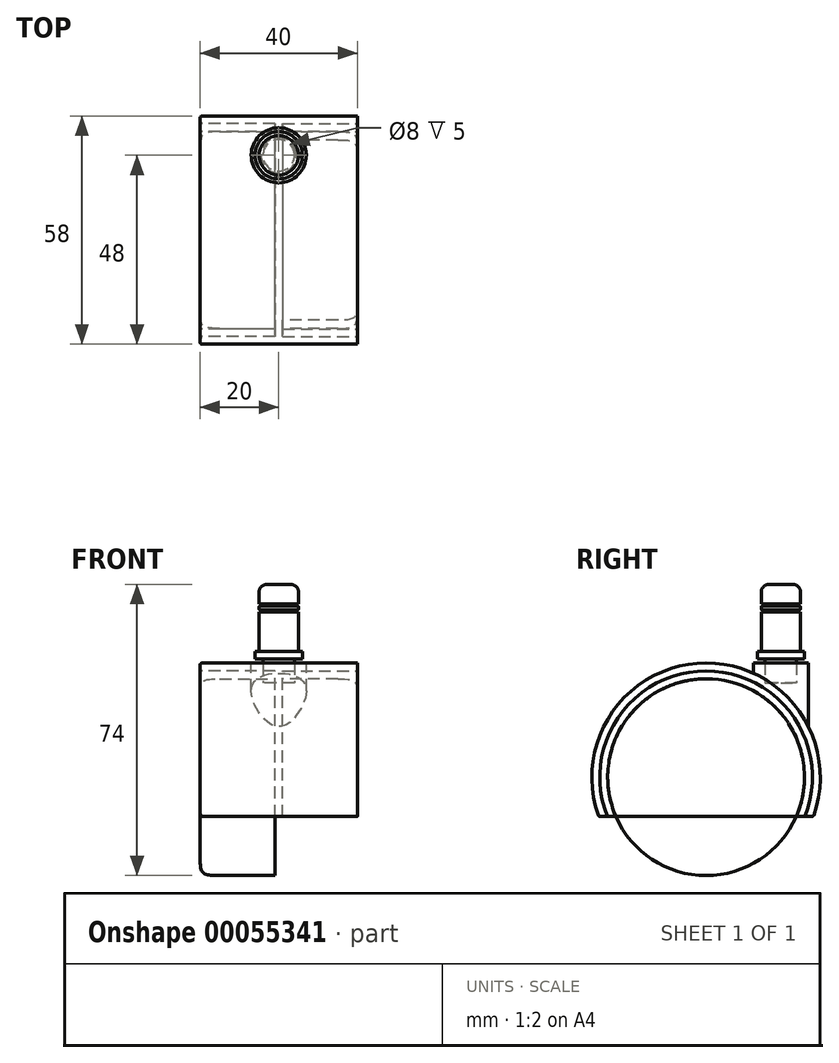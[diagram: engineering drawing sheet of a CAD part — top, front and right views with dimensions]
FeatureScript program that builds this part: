
annotation { "Feature Type Name" : "Feature", "Feature Type Description" : "" }
export const myFeature = defineFeature(function(context is Context, id is Id, definition is map)
    precondition{}
    {
        {
            var Q0;
            Q0=qCreatedBy(makeId("Top.planeOp"),FACE);
            var sketch = newSketch(context, id + "F0", { "sketchPlane" : qUnion([Q0])});
            skLineSegment(sketch, "E0.rect.bottom", {"start": v(20, -29) * mm, "end": v(-20, -29) * mm});
            skLineSegment(sketch, "E0.rect.top", {"start": v(20, 29) * mm, "end": v(-20, 29) * mm});
            skLineSegment(sketch, "E0.rect.left", {"start": v(20, -29) * mm, "end": v(20, 29) * mm});
            skLineSegment(sketch, "E0.rect.right", {"start": v(-20, -29) * mm, "end": v(-20, 29) * mm});
            skPoint(sketch, "E0.rect.middle", {"position": v(0, 0) * mm});
            skLineSegment(sketch, "E1", {"start": v(0, 0) * mm, "end": v(0, 19) * mm, "construction": true});
            skCircle(sketch, "E2", {"center": v(0, 19) * mm, "radius": 7 * mm});
            skSolve(sketch);
        }
        {
            var Q0;
            Q0=makeQuery(id+"F0.imprint","IMPRINT",FACE,{"disambiguationData":[TD([[makeQuery(id+"F0.imprint","IMPRINT",EDGE,{"derivedFrom":sQuery(id+"F0.wireOp",EDGE,"E0.rect.bottom")}),-1.0]])]});
            var Q1;
            Q1=makeQuery(id+"F0.imprint","IMPRINT",FACE,{"disambiguationData":[TD([[makeQuery(id+"F0.imprint","IMPRINT",EDGE,{"derivedFrom":sQuery(id+"F0.wireOp",EDGE,"E2")}),1.0]])]});
            extrude(context, id + "F1", {"entities" : qUnion([Q0, Q1]), "oppositeDirection" : true, "depth" : 50 * mm});
        }
        {
            var Q0;
            Q0=makeQuery(id+"F1.opExtrude","SWEPT_FACE",FACE,{"disambiguationData":[OSD([sQuery(id+"F0.wireOp",EDGE,"E0.rect.left")])]});
            var sketch = newSketch(context, id + "F2", { "sketchPlane" : qUnion([Q0])});
            skLineSegment(sketch, "E3", {"start": v(0, 0) * mm, "end": v(0, -29) * mm, "construction": true});
            skPoint(sketch, "E3.endSnap0", {"position": v(0, 0) * mm});
            skCircle(sketch, "E4", {"center": v(0, -29) * mm, "radius": 29 * mm});
            skCircle(sketch, "E5", {"center": v(0, -29) * mm, "radius": 27 * mm});
            skLineSegment(sketch, "E6", {"start": v(0, -29) * mm, "end": v(0, -39) * mm, "construction": true});
            skLineSegment(sketch, "E7", {"start": v(0, -39) * mm, "end": v(-27.22, -39) * mm});
            skLineSegment(sketch, "E8", {"start": v(0, -39) * mm, "end": v(27.22, -39) * mm});
            skSolve(sketch);
        }
        {
            var Q0;
            {var subQ0=sQuery(id+"F2.wireOp",EDGE,"E4");var subQ1=sQuery(id+"F0.wireOp",EDGE,"E0.rect.left");var subQ2=makeQuery(id+"F1.opExtrude","CAP_EDGE",EDGE,{"disambiguationData":[OSD([subQ1])],"isStart":true});var subQ3=makeQuery(id+"F2.imprint","INTERSECT",VERTEX,{"derivedFrom":[subQ2,subQ0]});Q0=makeQuery(id+"F2.imprint","IMPRINT",FACE,{"disambiguationData":[TD([[makeQuery(id+"F2.imprint","IMPRINT",EDGE,{"disambiguationData":[TD([[subQ3,-1.0]])],"derivedFrom":subQ0}),-1.0]])]});}
            var Q1;
            {var subQ0=sQuery(id+"F2.wireOp",EDGE,"E4");var subQ1=sQuery(id+"F0.wireOp",EDGE,"E0.rect.left");var subQ2=makeQuery(id+"F1.opExtrude","CAP_EDGE",EDGE,{"disambiguationData":[OSD([subQ1])],"isStart":true});var subQ3=makeQuery(id+"F2.imprint","INTERSECT",VERTEX,{"derivedFrom":[subQ2,subQ0]});Q1=makeQuery(id+"F2.imprint","IMPRINT",FACE,{"disambiguationData":[TD([[makeQuery(id+"F2.imprint","IMPRINT",EDGE,{"disambiguationData":[TD([[subQ3,1.0]])],"derivedFrom":subQ0}),-1.0]])]});}
            var Q2;
            {var subQ0=sQuery(id+"F2.wireOp",EDGE,"E4");var subQ1=makeQuery(id+"F2.imprint","INTERSECT",VERTEX,{"derivedFrom":[subQ0,sQuery(id+"F2.wireOp",EDGE,"E8")]});Q2=makeQuery(id+"F2.imprint","IMPRINT",FACE,{"disambiguationData":[TD([[makeQuery(id+"F2.imprint","IMPRINT",EDGE,{"disambiguationData":[TD([[subQ1,1.0]])],"derivedFrom":subQ0}),-1.0]])]});}
            var Q3;
            {var subQ0=sQuery(id+"F2.wireOp",EDGE,"E4");var subQ1=makeQuery(id+"F2.imprint","INTERSECT",VERTEX,{"derivedFrom":[subQ0,sQuery(id+"F2.wireOp",EDGE,"E7")]});Q3=makeQuery(id+"F2.imprint","IMPRINT",FACE,{"disambiguationData":[TD([[makeQuery(id+"F2.imprint","IMPRINT",EDGE,{"disambiguationData":[TD([[subQ1,-1.0]])],"derivedFrom":subQ0}),-1.0]])]});}
            var Q4;
            {var subQ1=sQuery(id+"F2.wireOp",EDGE,"E7");var subQ3=sQuery(id+"F2.wireOp",EDGE,"E5");var subQ4=makeQuery(id+"F2.imprint","INTERSECT",VERTEX,{"derivedFrom":[subQ3,subQ1]});Q4=makeQuery(id+"F2.imprint","IMPRINT",FACE,{"disambiguationData":[TD([[makeQuery(id+"F2.imprint","IMPRINT",EDGE,{"disambiguationData":[TD([[subQ4,-1.0]])],"derivedFrom":subQ3}),1.0]])]});}
            var Q5;
            {var subQ0=sQuery(id+"F2.wireOp",EDGE,"E7");var subQ1=sQuery(id+"F2.wireOp",EDGE,"E4");var subQ2=makeQuery(id+"F2.imprint","INTERSECT",VERTEX,{"derivedFrom":[subQ1,subQ0]});Q5=makeQuery(id+"F2.imprint","IMPRINT",FACE,{"disambiguationData":[TD([[makeQuery(id+"F2.imprint","IMPRINT",EDGE,{"disambiguationData":[TD([[subQ2,-1.0]])],"derivedFrom":subQ1}),1.0]])]});}
            var Q6;
            {var subQ0=sQuery(id+"F2.wireOp",EDGE,"E8");var subQ1=sQuery(id+"F2.wireOp",EDGE,"E4");var subQ2=makeQuery(id+"F2.imprint","INTERSECT",VERTEX,{"derivedFrom":[subQ1,subQ0]});Q6=makeQuery(id+"F2.imprint","IMPRINT",FACE,{"disambiguationData":[TD([[makeQuery(id+"F2.imprint","IMPRINT",EDGE,{"disambiguationData":[TD([[subQ2,1.0]])],"derivedFrom":subQ1}),1.0]])]});}
            extrude(context, id + "F3", {"entities" : qUnion([Q0, Q1, Q2, Q3, Q4, Q5, Q6]), "operationType" : NewBodyOperationType.REMOVE, "endBound" : BoundingType.THROUGH_ALL, "oppositeDirection" : true, "depth" : 25 * mm});
        }
        {
            var Q0;
            Q0=makeQuery(id+"F1.opExtrude","SWEPT_FACE",FACE,{"disambiguationData":[OSD([sQuery(id+"F0.wireOp",EDGE,"E0.rect.right")])]});
            var sketch = newSketch(context, id + "F4", { "sketchPlane" : qUnion([Q0])});
            skCircle(sketch, "E9", {"center": v(0, -29) * mm, "radius": 27 * mm});
            skSolve(sketch);
        }
        {
            var Q0;
            Q0=makeQuery(id+"F0.imprint","IMPRINT",FACE,{"disambiguationData":[TD([[makeQuery(id+"F0.imprint","IMPRINT",EDGE,{"derivedFrom":sQuery(id+"F0.wireOp",EDGE,"E2")}),1.0]])]});
            extrude(context, id + "F5", {"entities" : qUnion([Q0]), "operationType" : NewBodyOperationType.ADD, "oppositeDirection" : true, "depth" : 25 * mm});
        }
        {
            var Q0;
            {var subQ0=sQuery(id+"F2.wireOp",EDGE,"E7");var subQ1=sQuery(id+"F2.wireOp",EDGE,"E5");var subQ2=makeQuery(id+"F2.imprint","INTERSECT",VERTEX,{"derivedFrom":[subQ1,subQ0]});Q0=makeQuery(id+"F2.imprint","IMPRINT",FACE,{"disambiguationData":[TD([[makeQuery(id+"F2.imprint","IMPRINT",EDGE,{"disambiguationData":[TD([[subQ2,1.0]])],"derivedFrom":subQ1}),1.0]])]});}
            extrude(context, id + "F6", {"entities" : qUnion([Q0]), "operationType" : NewBodyOperationType.REMOVE, "oppositeDirection" : true, "depth" : 19 * mm});
        }
        {
            var Q0;
            {var subQ0=sQuery(id+"F4.wireOp",EDGE,"E9");var subQ1=makeQuery(id+"F3.boolean.opBoolean","INTERSECT",EDGE,{"derivedFrom":[makeQuery(id+"F1.opExtrude","SWEPT_FACE",FACE,{"disambiguationData":[OSD([sQuery(id+"F0.wireOp",EDGE,"E0.rect.right")])]}),makeQuery(id+"F3.opExtrude","SWEPT_FACE",FACE,{"disambiguationData":[OSD([sQuery(id+"F2.wireOp",EDGE,"E7"),sQuery(id+"F2.wireOp",EDGE,"E8")])]})]});var subQ2=makeQuery(id+"F4.imprint","INTERSECT",VERTEX,{"disambiguationData":[OD(0.0)],"derivedFrom":[subQ1,subQ0]});Q0=makeQuery(id+"F4.imprint","IMPRINT",FACE,{"disambiguationData":[TD([[makeQuery(id+"F4.imprint","IMPRINT",EDGE,{"disambiguationData":[TD([[subQ2,-1.0]])],"derivedFrom":subQ0}),1.0]])]});}
            extrude(context, id + "F7", {"entities" : qUnion([Q0]), "operationType" : NewBodyOperationType.REMOVE, "oppositeDirection" : true, "depth" : 19 * mm});
        }
        {
            var Q0;
            Q0=makeQuery(id+"F6.boolean.opBoolean","COPY",FACE,{"derivedFrom":makeQuery(id+"F6.opExtrude","CAP_FACE",FACE,{"disambiguationData":[OSD([sQuery(id+"F2.wireOp",EDGE,"E5"),sQuery(id+"F2.wireOp",EDGE,"E7"),sQuery(id+"F2.wireOp",EDGE,"E8")])],"isStart":false})});
            var sketch = newSketch(context, id + "F8", { "sketchPlane" : qUnion([Q0])});
            skCircle(sketch, "E10", {"center": v(0, -29) * mm, "radius": 25 * mm});
            skCircle(sketch, "E11", {"center": v(0, -29) * mm, "radius": 5 * mm});
            skSolve(sketch);
        }
        {
            var Q0;
            Q0=makeQuery(id+"F8.imprint","IMPRINT",FACE,{"disambiguationData":[TD([[makeQuery(id+"F8.imprint","IMPRINT",EDGE,{"derivedFrom":sQuery(id+"F8.wireOp",EDGE,"E11")}),1.0]])]});
            extrude(context, id + "F9", {"entities" : qUnion([Q0]), "operationType" : NewBodyOperationType.REMOVE, "endBound" : BoundingType.THROUGH_ALL, "oppositeDirection" : true, "depth" : 25 * mm});
        }
        {
            var Q0;
            Q0=makeQuery(id+"F8.imprint","IMPRINT",FACE,{"disambiguationData":[TD([[makeQuery(id+"F8.imprint","IMPRINT",EDGE,{"derivedFrom":sQuery(id+"F8.wireOp",EDGE,"E11")}),-1.0]])]});
            var Q1;
            Q1=makeQuery(id+"F8.imprint","IMPRINT",FACE,{"disambiguationData":[TD([[makeQuery(id+"F8.imprint","IMPRINT",EDGE,{"derivedFrom":sQuery(id+"F8.wireOp",EDGE,"E11")}),1.0]])]});
            var Q2;
            {var subQ0=sQuery(id+"F8.wireOp",EDGE,"E10");var subQ1=makeQuery(id+"F6.boolean.opBoolean","COPY",EDGE,{"derivedFrom":makeQuery(id+"F6.opExtrude","CAP_EDGE",EDGE,{"disambiguationData":[OSD([sQuery(id+"F2.wireOp",EDGE,"E7"),sQuery(id+"F2.wireOp",EDGE,"E8")])],"isStart":false})});var subQ2=makeQuery(id+"F8.imprint","INTERSECT",VERTEX,{"disambiguationData":[OD(0.0)],"derivedFrom":[subQ1,subQ0]});Q2=makeQuery(id+"F8.imprint","IMPRINT",FACE,{"disambiguationData":[TD([[makeQuery(id+"F8.imprint","IMPRINT",EDGE,{"disambiguationData":[TD([[subQ2,-1.0]])],"derivedFrom":subQ0}),1.0]])]});}
            extrude(context, id + "F10", {"entities" : qUnion([Q0, Q1, Q2]), "depth" : 19 * mm});
        }
        {
            var Q0;
            Q0=makeQuery(id+"F8.imprint","IMPRINT",FACE,{"disambiguationData":[TD([[makeQuery(id+"F8.imprint","IMPRINT",EDGE,{"derivedFrom":sQuery(id+"F8.wireOp",EDGE,"E11")}),1.0]])]});
            extrude(context, id + "F11", {"entities" : qUnion([Q0]), "operationType" : NewBodyOperationType.ADD, "oppositeDirection" : true, "depth" : 2 * mm});
        }
        {
            var Q0;
            Q0=makeQuery(id+"F11.opExtrude","CAP_FACE",FACE,{"disambiguationData":[OSD([sQuery(id+"F8.wireOp",EDGE,"E11")])],"isStart":false});
            var sketch = newSketch(context, id + "F12", { "sketchPlane" : qUnion([Q0])});
            skCircle(sketch, "E12", {"center": v(0, -29) * mm, "radius": 25 * mm});
            skSolve(sketch);
        }
        {
            var Q0;
            Q0=makeQuery(id+"F12.imprint","IMPRINT",FACE,{"disambiguationData":[TD([[makeQuery(id+"F12.imprint","IMPRINT",EDGE,{"derivedFrom":sQuery(id+"F12.wireOp",EDGE,"E12")}),1.0]])]});
            var Q1;
            Q1=makeQuery(id+"F12.imprint","IMPRINT",FACE,{"disambiguationData":[TD([[makeQuery(id+"F12.imprint","IMPRINT",EDGE,{"derivedFrom":makeQuery(id+"F11.opExtrude","CAP_EDGE",EDGE,{"disambiguationData":[OSD([sQuery(id+"F8.wireOp",EDGE,"E11")])],"isStart":false})}),-1.0]])]});
            extrude(context, id + "F13", {"entities" : qUnion([Q0, Q1]), "operationType" : NewBodyOperationType.ADD, "depth" : 19 * mm});
        }
        {
            var Q0;
            {var subQ0=sQuery(id+"F2.wireOp",EDGE,"E4");var subQ1=sQuery(id+"F0.wireOp",EDGE,"E0.rect.left");var subQ4=makeQuery(id+"F2.imprint","INTERSECT",VERTEX,{"derivedFrom":[makeQuery(id+"F1.opExtrude","CAP_EDGE",EDGE,{"disambiguationData":[OSD([subQ1])],"isStart":true}),subQ0]});Q0=makeQuery(id+"F3.boolean.opBoolean","TWEAK_EDGE",EDGE,{"derivedFrom":[makeQuery(id+"F3.opExtrude","CAP_EDGE",EDGE,{"disambiguationData":[OSD([subQ0]),TDD([makeQuery(id+"F2.imprint","IMPRINT",EDGE,{"disambiguationData":[TD([[subQ4,1.0]])],"derivedFrom":subQ0})])],"isStart":true}),makeQuery(id+"F3.opExtrude","CAP_EDGE",EDGE,{"disambiguationData":[OSD([subQ0]),TDD([makeQuery(id+"F2.imprint","IMPRINT",EDGE,{"disambiguationData":[TD([[subQ4,-1.0]])],"derivedFrom":subQ0})])],"isStart":true}),makeQuery(id+"F3.opExtrude","CAP_EDGE",EDGE,{"disambiguationData":[OSD([subQ0]),TDD([makeQuery(id+"F2.imprint","IMPRINT",EDGE,{"disambiguationData":[TD([[makeQuery(id+"F2.imprint","INTERSECT",VERTEX,{"derivedFrom":[subQ0,sQuery(id+"F2.wireOp",EDGE,"E7")]}),1.0]])],"derivedFrom":subQ0})])],"isStart":true}),makeQuery(id+"F3.opExtrude","CAP_EDGE",EDGE,{"disambiguationData":[OSD([subQ0]),TDD([makeQuery(id+"F2.imprint","IMPRINT",EDGE,{"disambiguationData":[TD([[makeQuery(id+"F2.imprint","INTERSECT",VERTEX,{"derivedFrom":[subQ0,sQuery(id+"F2.wireOp",EDGE,"E8")]}),-1.0]])],"derivedFrom":subQ0})])],"isStart":true})]});}
            var Q1;
            Q1=makeQuery(id+"F3.boolean.opBoolean","COPY",EDGE,{"derivedFrom":makeQuery(id+"F3.opExtrude","SWEPT_EDGE",EDGE,{"disambiguationData":[OSD([sQuery(id+"F2.wireOp",EDGE,"E4"),sQuery(id+"F2.wireOp",EDGE,"E7")])]})});
            var Q2;
            {var subQ0=sQuery(id+"F2.wireOp",EDGE,"E4");var subQ1=sQuery(id+"F0.wireOp",EDGE,"E0.rect.left");var subQ4=makeQuery(id+"F2.imprint","INTERSECT",VERTEX,{"derivedFrom":[makeQuery(id+"F1.opExtrude","CAP_EDGE",EDGE,{"disambiguationData":[OSD([subQ1])],"isStart":true}),subQ0]});Q2=makeQuery(id+"F3.boolean.opBoolean","INTERSECT",EDGE,{"derivedFrom":[makeQuery(id+"F1.opExtrude","SWEPT_FACE",FACE,{"disambiguationData":[OSD([sQuery(id+"F0.wireOp",EDGE,"E0.rect.right")])]}),makeQuery(id+"F3.opExtrude","SWEPT_FACE",FACE,{"disambiguationData":[OSD([subQ0]),TDD([makeQuery(id+"F2.imprint","IMPRINT",EDGE,{"disambiguationData":[TD([[subQ4,1.0]])],"derivedFrom":subQ0})])]}),makeQuery(id+"F3.opExtrude","SWEPT_FACE",FACE,{"disambiguationData":[OSD([subQ0]),TDD([makeQuery(id+"F2.imprint","IMPRINT",EDGE,{"disambiguationData":[TD([[subQ4,-1.0]])],"derivedFrom":subQ0})])]}),makeQuery(id+"F3.opExtrude","SWEPT_FACE",FACE,{"disambiguationData":[OSD([subQ0]),TDD([makeQuery(id+"F2.imprint","IMPRINT",EDGE,{"disambiguationData":[TD([[makeQuery(id+"F2.imprint","INTERSECT",VERTEX,{"derivedFrom":[subQ0,sQuery(id+"F2.wireOp",EDGE,"E7")]}),1.0]])],"derivedFrom":subQ0})])]}),makeQuery(id+"F3.opExtrude","SWEPT_FACE",FACE,{"disambiguationData":[OSD([subQ0]),TDD([makeQuery(id+"F2.imprint","IMPRINT",EDGE,{"disambiguationData":[TD([[makeQuery(id+"F2.imprint","INTERSECT",VERTEX,{"derivedFrom":[subQ0,sQuery(id+"F2.wireOp",EDGE,"E8")]}),-1.0]])],"derivedFrom":subQ0})])]})]});}
            var Q3;
            Q3=makeQuery(id+"F3.boolean.opBoolean","COPY",EDGE,{"derivedFrom":makeQuery(id+"F3.opExtrude","SWEPT_EDGE",EDGE,{"disambiguationData":[OSD([sQuery(id+"F2.wireOp",EDGE,"E4"),sQuery(id+"F2.wireOp",EDGE,"E8")])]})});
            var Q4;
            Q4=makeQuery(id+"F7.boolean.opBoolean","COPY",EDGE,{"derivedFrom":makeQuery(id+"F7.opExtrude","CAP_EDGE",EDGE,{"disambiguationData":[OSD([sQuery(id+"F4.wireOp",EDGE,"E9")])],"isStart":true})});
            var Q5;
            Q5=makeQuery(id+"F6.boolean.opBoolean","COPY",EDGE,{"derivedFrom":makeQuery(id+"F6.opExtrude","CAP_EDGE",EDGE,{"disambiguationData":[OSD([sQuery(id+"F2.wireOp",EDGE,"E5")])],"isStart":true})});
            var Q6;
            Q6=makeQuery(id+"F6.boolean.opBoolean","COPY",EDGE,{"derivedFrom":makeQuery(id+"F6.opExtrude","SWEPT_EDGE",EDGE,{"disambiguationData":[OSD([sQuery(id+"F2.wireOp",EDGE,"E5"),sQuery(id+"F2.wireOp",EDGE,"E8")])]})});
            var Q7;
            {var subQ0=sQuery(id+"F4.wireOp",EDGE,"E9");var subQ1=sQuery(id+"F2.wireOp",EDGE,"E8");var subQ2=sQuery(id+"F2.wireOp",EDGE,"E7");var subQ3=sQuery(id+"F0.wireOp",EDGE,"E0.rect.right");Q7=makeQuery(id+"F7.boolean.opBoolean","COPY",EDGE,{"derivedFrom":makeQuery(id+"F7.opExtrude","SWEPT_EDGE",EDGE,{"disambiguationData":[OSD([subQ3,subQ2,subQ1,subQ0]),TDD([makeQuery(id+"F4.imprint","INTERSECT",VERTEX,{"disambiguationData":[OD(1.0)],"derivedFrom":[makeQuery(id+"F3.boolean.opBoolean","INTERSECT",EDGE,{"derivedFrom":[makeQuery(id+"F1.opExtrude","SWEPT_FACE",FACE,{"disambiguationData":[OSD([subQ3])]}),makeQuery(id+"F3.opExtrude","SWEPT_FACE",FACE,{"disambiguationData":[OSD([subQ2,subQ1])]})]}),subQ0]})])]})});}
            var Q8;
            {var subQ0=sQuery(id+"F4.wireOp",EDGE,"E9");var subQ1=sQuery(id+"F2.wireOp",EDGE,"E8");var subQ2=sQuery(id+"F2.wireOp",EDGE,"E7");var subQ3=sQuery(id+"F0.wireOp",EDGE,"E0.rect.right");Q8=makeQuery(id+"F7.boolean.opBoolean","COPY",EDGE,{"derivedFrom":makeQuery(id+"F7.opExtrude","SWEPT_EDGE",EDGE,{"disambiguationData":[OSD([subQ3,subQ2,subQ1,subQ0]),TDD([makeQuery(id+"F4.imprint","INTERSECT",VERTEX,{"disambiguationData":[OD(0.0)],"derivedFrom":[makeQuery(id+"F3.boolean.opBoolean","INTERSECT",EDGE,{"derivedFrom":[makeQuery(id+"F1.opExtrude","SWEPT_FACE",FACE,{"disambiguationData":[OSD([subQ3])]}),makeQuery(id+"F3.opExtrude","SWEPT_FACE",FACE,{"disambiguationData":[OSD([subQ2,subQ1])]})]}),subQ0]})])]})});}
            var Q9;
            Q9=makeQuery(id+"F6.boolean.opBoolean","COPY",EDGE,{"derivedFrom":makeQuery(id+"F6.opExtrude","SWEPT_EDGE",EDGE,{"disambiguationData":[OSD([sQuery(id+"F2.wireOp",EDGE,"E5"),sQuery(id+"F2.wireOp",EDGE,"E7")])]})});
            fillet(context, id + "F14", {"entities" : qUnion([Q0, Q1, Q2, Q3, Q4, Q5, Q6, Q7, Q8, Q9]), "radius" : 0.5 * mm, "tangentPropagation" : true, "allowEdgeOverflow" : false});
        }
        {
            var Q0;
            Q0=makeQuery(id+"F10.opExtrude","CAP_EDGE",EDGE,{"disambiguationData":[OSD([sQuery(id+"F8.wireOp",EDGE,"E10")])],"isStart":false});
            var Q1;
            Q1=makeQuery(id+"F13.opExtrude","CAP_EDGE",EDGE,{"disambiguationData":[OSD([sQuery(id+"F12.wireOp",EDGE,"E12")])],"isStart":false});
            fillet(context, id + "F15", {"entities" : qUnion([Q0, Q1]), "radius" : 5 * mm, "rho" : 0.7, "crossSection" : FilletCrossSection.CONIC, "allowEdgeOverflow" : false});
        }
        {
            var Q0;
            Q0=makeQuery(id+"F5.opExtrude","CAP_FACE",FACE,{"disambiguationData":[OSD([sQuery(id+"F0.wireOp",EDGE,"E2")])],"isStart":true});
            var sketch = newSketch(context, id + "F16", { "sketchPlane" : qUnion([Q0])});
            skCircle(sketch, "E13", {"center": v(0, 19) * mm, "radius": 4 * mm});
            skSolve(sketch);
        }
        {
            var Q0;
            Q0=makeQuery(id+"F16.imprint","IMPRINT",FACE,{"disambiguationData":[TD([[makeQuery(id+"F16.imprint","IMPRINT",EDGE,{"derivedFrom":sQuery(id+"F16.wireOp",EDGE,"E13")}),1.0]])]});
            extrude(context, id + "F17", {"entities" : qUnion([Q0]), "operationType" : NewBodyOperationType.REMOVE, "oppositeDirection" : true, "depth" : 5 * mm});
        }
        {
            var Q0;
            Q0=makeQuery(id+"F17.boolean.opBoolean","COPY",FACE,{"derivedFrom":makeQuery(id+"F17.opExtrude","CAP_FACE",FACE,{"disambiguationData":[OSD([sQuery(id+"F16.wireOp",EDGE,"E13")])],"isStart":false})});
            extrude(context, id + "F18", {"entities" : qUnion([Q0]), "depth" : 6 * mm});
        }
        {
            var Q0;
            Q0=makeQuery(id+"F18.opExtrude","CAP_FACE",FACE,{"disambiguationData":[OSD([sQuery(id+"F16.wireOp",EDGE,"E13")])],"isStart":false});
            var sketch = newSketch(context, id + "F19", { "sketchPlane" : qUnion([Q0])});
            skCircle(sketch, "E14", {"center": v(0, 19) * mm, "radius": 6 * mm});
            skSolve(sketch);
        }
        {
            var Q0;
            Q0=makeQuery(id+"F19.imprint","IMPRINT",FACE,{"disambiguationData":[TD([[makeQuery(id+"F19.imprint","IMPRINT",EDGE,{"derivedFrom":sQuery(id+"F19.wireOp",EDGE,"E14")}),1.0]])]});
            var Q1;
            Q1=makeQuery(id+"F19.imprint","IMPRINT",FACE,{"disambiguationData":[TD([[makeQuery(id+"F19.imprint","IMPRINT",EDGE,{"derivedFrom":makeQuery(id+"F18.opExtrude","CAP_EDGE",EDGE,{"disambiguationData":[OSD([sQuery(id+"F16.wireOp",EDGE,"E13")])],"isStart":false})}),1.0]])]});
            extrude(context, id + "F20", {"entities" : qUnion([Q0, Q1]), "operationType" : NewBodyOperationType.ADD, "depth" : 2 * mm});
        }
        {
            var Q0;
            Q0=makeQuery(id+"F20.opExtrude","CAP_FACE",FACE,{"disambiguationData":[OSD([sQuery(id+"F19.wireOp",EDGE,"E14")])],"isStart":false});
            var sketch = newSketch(context, id + "F21", { "sketchPlane" : qUnion([Q0])});
            skCircle(sketch, "E15", {"center": v(0, 19) * mm, "radius": 5 * mm});
            skSolve(sketch);
        }
        {
            var Q0;
            Q0=makeQuery(id+"F21.imprint","IMPRINT",FACE,{"disambiguationData":[TD([[makeQuery(id+"F21.imprint","IMPRINT",EDGE,{"derivedFrom":sQuery(id+"F21.wireOp",EDGE,"E15")}),1.0]])]});
            extrude(context, id + "F22", {"entities" : qUnion([Q0]), "operationType" : NewBodyOperationType.ADD, "depth" : 10 * mm});
        }
        {
            var Q0;
            Q0=makeQuery(id+"F22.opExtrude","CAP_FACE",FACE,{"disambiguationData":[OSD([sQuery(id+"F21.wireOp",EDGE,"E15")])],"isStart":false});
            var sketch = newSketch(context, id + "F23", { "sketchPlane" : qUnion([Q0])});
            skCircle(sketch, "E16", {"center": v(0, 19) * mm, "radius": 4.5 * mm});
            skSolve(sketch);
        }
        {
            var Q0;
            Q0=makeQuery(id+"F23.imprint","IMPRINT",FACE,{"disambiguationData":[TD([[makeQuery(id+"F23.imprint","IMPRINT",EDGE,{"derivedFrom":sQuery(id+"F23.wireOp",EDGE,"E16")}),1.0]])]});
            extrude(context, id + "F24", {"entities" : qUnion([Q0]), "operationType" : NewBodyOperationType.ADD, "depth" : 0.5 * mm});
        }
        {
            var Q0;
            Q0=makeQuery(id+"F24.opExtrude","CAP_FACE",FACE,{"disambiguationData":[OSD([sQuery(id+"F23.wireOp",EDGE,"E16")])],"isStart":false});
            var sketch = newSketch(context, id + "F25", { "sketchPlane" : qUnion([Q0])});
            skCircle(sketch, "E17", {"center": v(0, 19) * mm, "radius": 5 * mm});
            skSolve(sketch);
        }
        {
            var Q0;
            Q0=makeQuery(id+"F25.imprint","IMPRINT",FACE,{"disambiguationData":[TD([[makeQuery(id+"F25.imprint","IMPRINT",EDGE,{"derivedFrom":makeQuery(id+"F24.opExtrude","CAP_EDGE",EDGE,{"disambiguationData":[OSD([sQuery(id+"F23.wireOp",EDGE,"E16")])],"isStart":false})}),1.0]])]});
            var Q1;
            Q1=makeQuery(id+"F25.imprint","IMPRINT",FACE,{"disambiguationData":[TD([[makeQuery(id+"F25.imprint","IMPRINT",EDGE,{"derivedFrom":sQuery(id+"F25.wireOp",EDGE,"E17")}),1.0]])]});
            extrude(context, id + "F26", {"entities" : qUnion([Q0, Q1]), "operationType" : NewBodyOperationType.ADD, "depth" : 1 * mm});
        }
        {
            var Q0;
            Q0=makeQuery(id+"F26.opExtrude","CAP_FACE",FACE,{"disambiguationData":[OSD([sQuery(id+"F25.wireOp",EDGE,"E17")])],"isStart":false});
            var sketch = newSketch(context, id + "F27", { "sketchPlane" : qUnion([Q0])});
            skCircle(sketch, "E18", {"center": v(0, 19) * mm, "radius": 4.5 * mm});
            skSolve(sketch);
        }
        {
            var Q0;
            Q0=makeQuery(id+"F27.imprint","IMPRINT",FACE,{"disambiguationData":[TD([[makeQuery(id+"F27.imprint","IMPRINT",EDGE,{"derivedFrom":sQuery(id+"F27.wireOp",EDGE,"E18")}),1.0]])]});
            extrude(context, id + "F28", {"entities" : qUnion([Q0]), "operationType" : NewBodyOperationType.ADD, "depth" : 0.5 * mm});
        }
        {
            var Q0;
            Q0=makeQuery(id+"F28.opExtrude","CAP_FACE",FACE,{"disambiguationData":[OSD([sQuery(id+"F27.wireOp",EDGE,"E18")])],"isStart":false});
            var sketch = newSketch(context, id + "F29", { "sketchPlane" : qUnion([Q0])});
            skCircle(sketch, "E19", {"center": v(0, 19) * mm, "radius": 5 * mm});
            skSolve(sketch);
        }
        {
            var Q0;
            Q0=makeQuery(id+"F29.imprint","IMPRINT",FACE,{"disambiguationData":[TD([[makeQuery(id+"F29.imprint","IMPRINT",EDGE,{"derivedFrom":makeQuery(id+"F28.opExtrude","CAP_EDGE",EDGE,{"disambiguationData":[OSD([sQuery(id+"F27.wireOp",EDGE,"E18")])],"isStart":false})}),1.0]])]});
            var Q1;
            Q1=makeQuery(id+"F29.imprint","IMPRINT",FACE,{"disambiguationData":[TD([[makeQuery(id+"F29.imprint","IMPRINT",EDGE,{"derivedFrom":sQuery(id+"F29.wireOp",EDGE,"E19")}),1.0]])]});
            extrude(context, id + "F30", {"entities" : qUnion([Q0, Q1]), "operationType" : NewBodyOperationType.ADD, "depth" : 5 * mm});
        }
        {
            var Q0;
            Q0=makeQuery(id+"F30.opExtrude","CAP_EDGE",EDGE,{"disambiguationData":[OSD([sQuery(id+"F29.wireOp",EDGE,"E19")])],"isStart":false});
            fillet(context, id + "F31", {"entities" : qUnion([Q0]), "radius" : 2 * mm, "tangentPropagation" : true, "allowEdgeOverflow" : false});
        }
        {
            var Q0;
            Q0=makeQuery(id+"F26.opExtrude","CAP_EDGE",EDGE,{"disambiguationData":[OSD([sQuery(id+"F25.wireOp",EDGE,"E17")])],"isStart":false});
            var Q1;
            Q1=makeQuery(id+"F26.opExtrude","CAP_EDGE",EDGE,{"disambiguationData":[OSD([sQuery(id+"F25.wireOp",EDGE,"E17")])],"isStart":true});
            fillet(context, id + "F32", {"entities" : qUnion([Q0, Q1]), "radius" : 0.3 * mm, "tangentPropagation" : true, "allowEdgeOverflow" : false});
        }
    });
